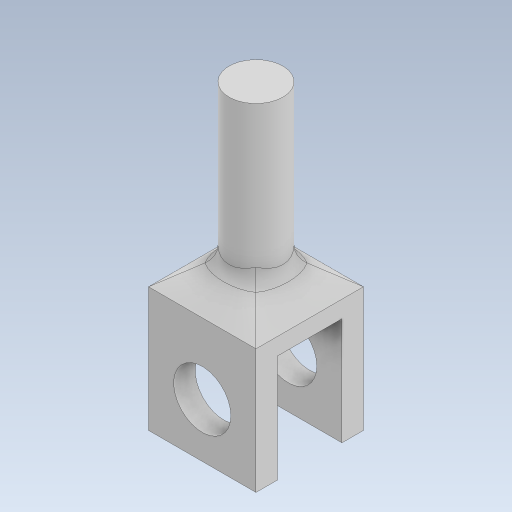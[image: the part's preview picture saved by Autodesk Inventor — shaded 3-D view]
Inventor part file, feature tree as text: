
AUTODESK INVENTOR PART (.ipt)
format: ipt  version: 2023 (Build 270158000, 158)  size: 226,304 bytes
history: native  units: in
note: dims shown in document units (in); Inventor stores cm internally (conversion verified against a paired STEP export)
features: sketch x4, extrude x3, other x2, plane x1, loft x1, hole x1, fillet x1
ambient origin geometry x8: Origin, YZ Plane, XZ Plane, XY Plane, X Axis, Y Axis, Z Axis, Center Point
bodies: Solid1 (feature_tree)
feature tree (13):
  extrude  "Extrusion1"  Depth=0.3in
  plane  "Work Plane1"
  extrude  "Extrusion2"  Depth=0.5in TaperAngle=0.0deg
  extrude  "Extrusion3"  Depth=0.2506in
  loft  "Loft3"
  hole  "Hole1"  [1 undecoded]
  fillet  "Fillet1"  [1 undecoded]
  sketch  "Sketch2"  dims[d0=0.1in d1=0.3in]
  sketch  "Sketch3"  dims[d2=0.5in d3=0.5in d4=0.0in]
  sketch  "Sketch4"  dims[d5=0.1969in d6=0.2506in]
  other  "Edges5"
  other  "Edges6"
  sketch  "Sketch7"  dims[d7=0.7087in d8=0.0in d17=0.0787in d18=0.0in d19=0.0in d20=90.0deg d21=0.0in d22=90.0deg d23=0.15in d34=0.266in d35=0.2362in d36=0.507in d37=0.0787in d38=0.5635in d39=0.5in d40=0.8108in d41=0.0787in]
note: 2 required parameter values undecoded (feature->parameter linkage not recoverable at this tier; creation-order binding heuristic only, values carry confidence <= 0.55)
